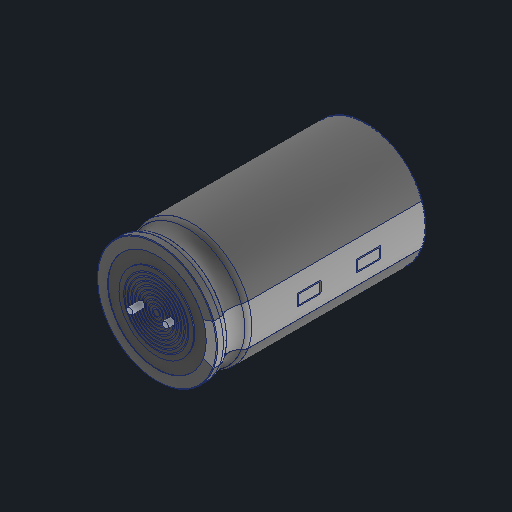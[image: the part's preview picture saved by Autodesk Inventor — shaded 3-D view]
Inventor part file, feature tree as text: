
AUTODESK INVENTOR PART (.ipt)
format: ipt  version: 2024 (Build 280153000, 153)  size: 534,528 bytes
history: native  units: mm
features: other x10, fillet x2
ambient origin geometry x8: Origin, YZ Plane, XZ Plane, XY Plane, X Axis, Y Axis, Z Axis, Center Point
bodies: Body1 (feature_tree), Body2 (feature_tree), Body3 (feature_tree), Body4 (feature_tree), Body5 (feature_tree), Body6 (feature_tree)
feature tree (12):
  other  "Твердое тело1"
  other  "Твердое тело2"
  other  "Твердое тело3"
  other  "Твердое тело4"
  other  "Твердое тело5"
  other  "Твердое тело6"
  other  "CROSS 2"
  other  "LEADS HOLES"
  other  "LEADS[2]"
  other  "2ND LEAD EXTENDED"
  fillet  "Fillet6"  [1 undecoded]
  fillet  "Fillet5"  [1 undecoded]
note: 2 required parameter values undecoded (feature->parameter linkage not recoverable at this tier; creation-order binding heuristic only, values carry confidence <= 0.55)
